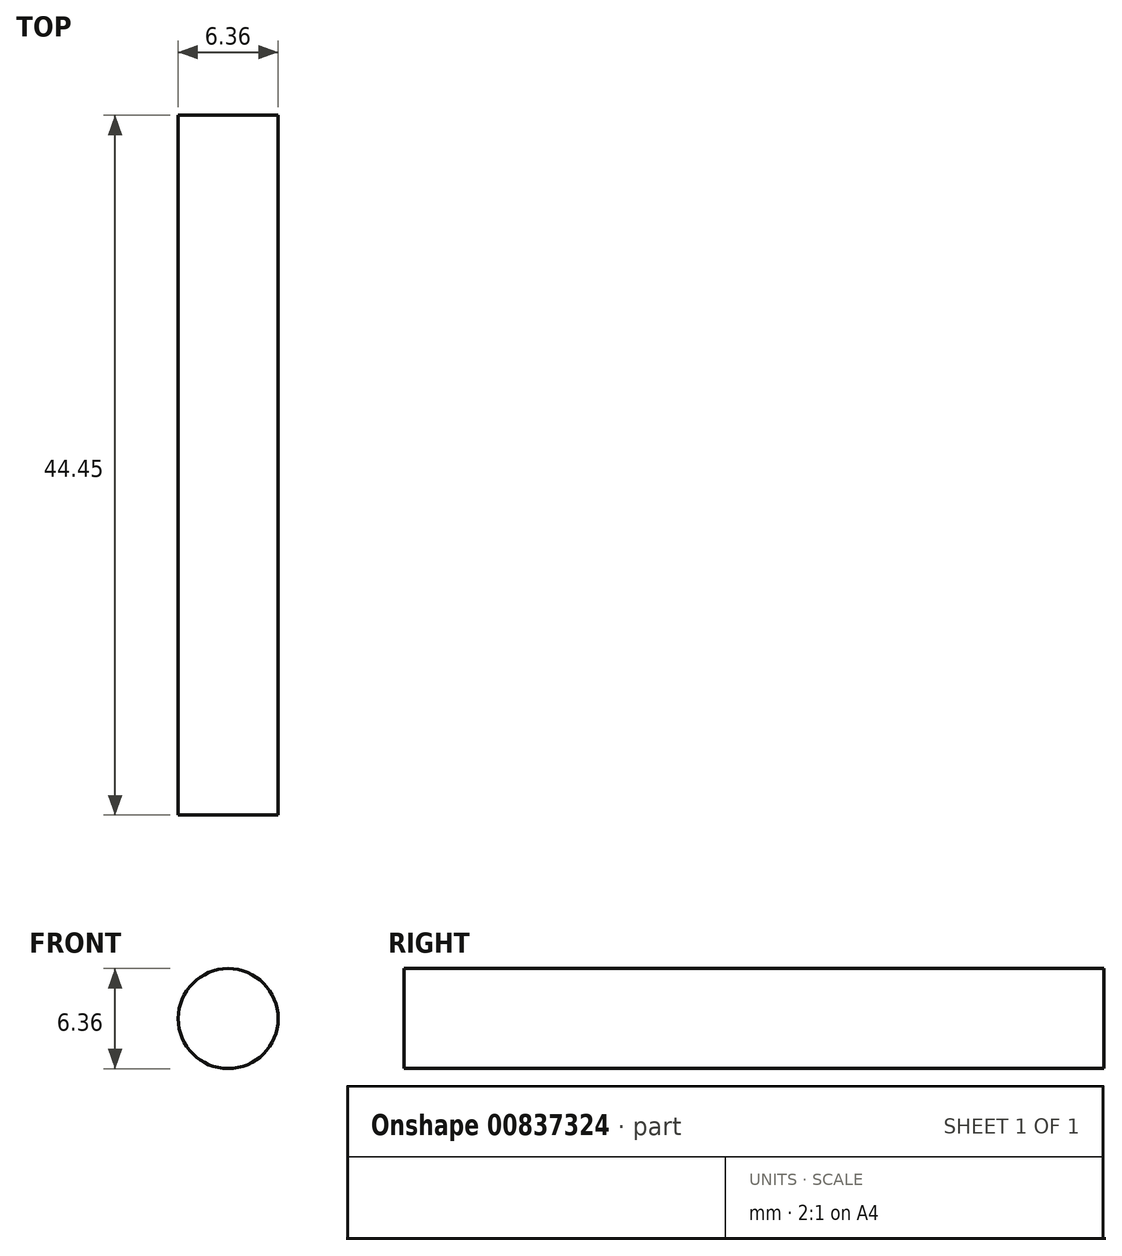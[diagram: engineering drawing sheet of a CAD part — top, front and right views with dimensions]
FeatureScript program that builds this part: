
annotation { "Feature Type Name" : "Feature", "Feature Type Description" : "" }
export const myFeature = defineFeature(function(context is Context, id is Id, definition is map)
    precondition{}
    {
        {
            var Q0;
            Q0=qCreatedBy(makeId("Front.planeOp"),FACE);
            var sketch = newSketch(context, id + "F0", { "sketchPlane" : qUnion([Q0])});
            skCircle(sketch, "E0", {"center": v(0, 0) * mm, "radius": 3.18 * mm});
            skSolve(sketch);
        }
        {
            var Q0;
            Q0=makeQuery(id+"F0.imprint","IMPRINT",FACE,{"disambiguationData":[TD([[makeQuery(id+"F0.imprint","IMPRINT",EDGE,{"derivedFrom":sQuery(id+"F0.wireOp",EDGE,"E0")}),1.0]])]});
            extrude(context, id + "F1", {"entities" : qUnion([Q0]), "depth" : 44.45 * mm, "offsetDistance" : 25.4 * mm});
        }
    });
